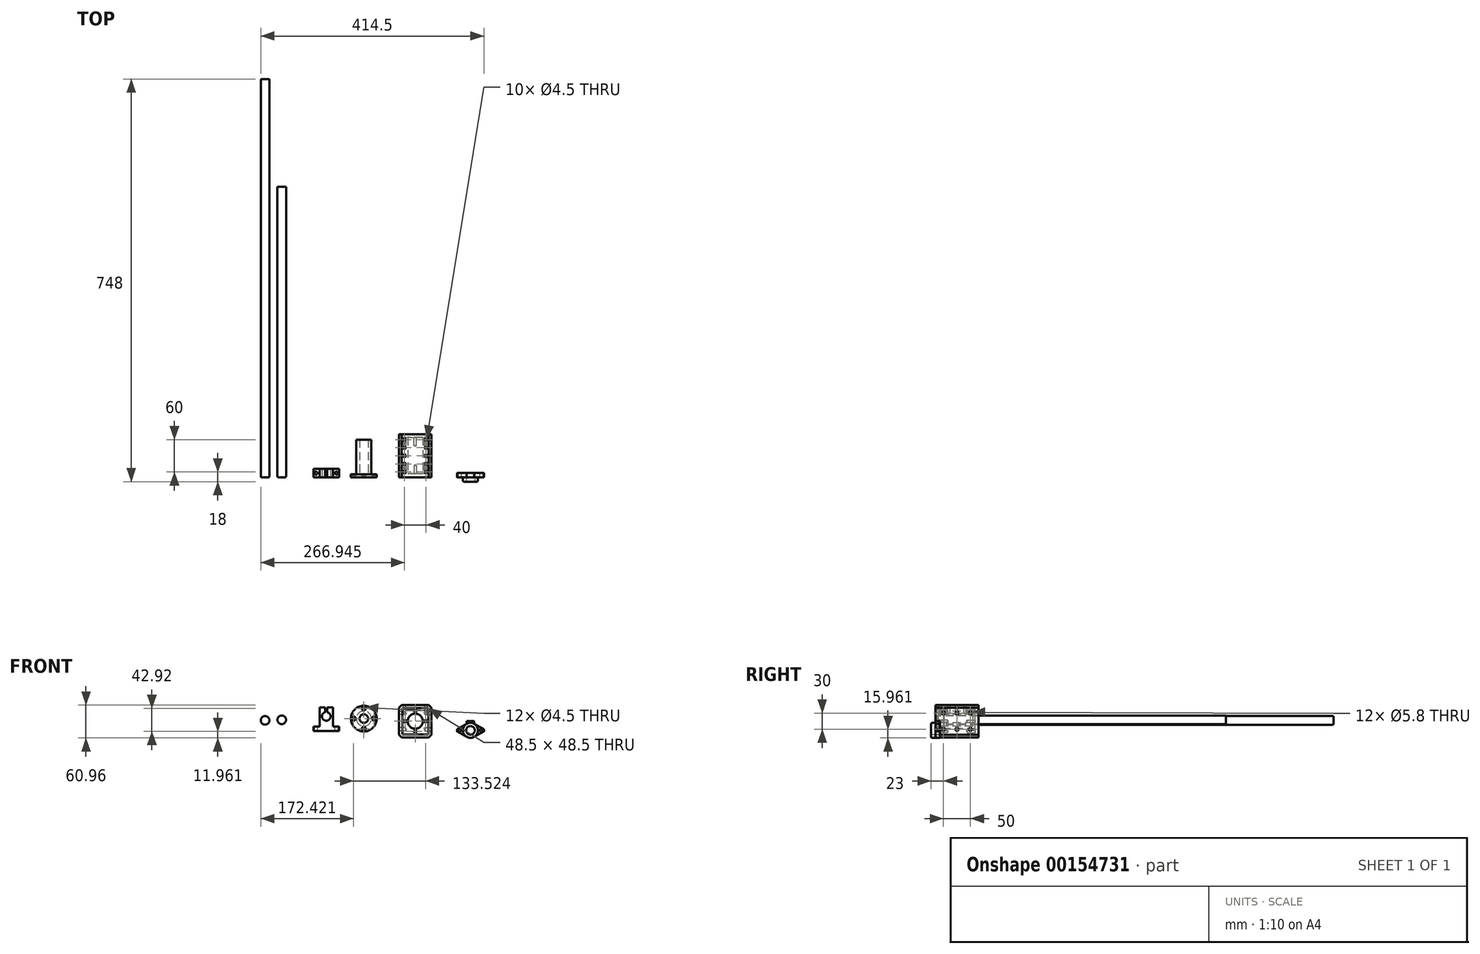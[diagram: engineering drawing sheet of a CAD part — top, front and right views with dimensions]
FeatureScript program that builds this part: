
annotation { "Feature Type Name" : "Feature", "Feature Type Description" : "" }
export const myFeature = defineFeature(function(context is Context, id is Id, definition is map)
    precondition{}
    {
        {
            var Q0;
            Q0=qCreatedBy(makeId("Front.planeOp"),FACE);
            var sketch = newSketch(context, id + "F0", { "sketchPlane" : qUnion([Q0])});
            skLineSegment(sketch, "E0.bottom", {"start": v(-58.78, 52.45) * mm, "end": v(-106.78, 52.45) * mm});
            skLineSegment(sketch, "E0.top", {"start": v(-58.78, 60.45) * mm, "end": v(-106.78, 60.45) * mm});
            skLineSegment(sketch, "E0.left", {"start": v(-58.78, 52.45) * mm, "end": v(-58.78, 60.45) * mm});
            skLineSegment(sketch, "E0.right", {"start": v(-106.78, 52.45) * mm, "end": v(-106.78, 60.45) * mm});
            skPoint(sketch, "E1.middle", {"position": v(-82.78, 52.45) * mm});
            skLineSegment(sketch, "E2.bottom", {"start": v(-70.28, 96.45) * mm, "end": v(-80.78, 96.45) * mm});
            skLineSegment(sketch, "E2.left", {"start": v(-70.28, 96.45) * mm, "end": v(-70.28, 60.45) * mm});
            skLineSegment(sketch, "E2.right", {"start": v(-95.28, 96.45) * mm, "end": v(-95.28, 60.45) * mm});
            skLineSegment(sketch, "E3", {"start": v(-82.78, 96.45) * mm, "end": v(-82.78, 52.45) * mm, "construction": true});
            skLineSegment(sketch, "E4.0", {"start": v(-58.78, 79.45) * mm, "end": v(-106.78, 79.45) * mm, "construction": true});
            skArc(sketch, "E5", {"start": v(-84.78, 87.2) * mm, "mid": v(-82.78, 71.45) * mm, "end": v(-80.78, 87.2) * mm});
            skLineSegment(sketch, "E6.0", {"start": v(-84.78, 87.2) * mm, "end": v(-84.78, 52.45) * mm, "construction": true});
            skLineSegment(sketch, "E7.0", {"start": v(-80.78, 87.2) * mm, "end": v(-80.78, 52.45) * mm, "construction": true});
            skLineSegment(sketch, "E8.trimOffspring", {"start": v(-84.78, 96.45) * mm, "end": v(-95.28, 96.45) * mm});
            skLineSegment(sketch, "E9", {"start": v(-80.78, 87.2) * mm, "end": v(-80.78, 96.45) * mm});
            skLineSegment(sketch, "E10", {"start": v(-84.78, 87.2) * mm, "end": v(-84.78, 96.45) * mm});
            skSolve(sketch);
        }
        {
            var Q0;
            Q0=makeQuery(id+"F0.imprint","IMPRINT",FACE,{"disambiguationData":[TD([[makeQuery(id+"F0.imprint","IMPRINT",EDGE,{"derivedFrom":sQuery(id+"F0.wireOp",EDGE,"E2.bottom")}),1.0]])]});
            var Q1;
            Q1=makeQuery(id+"F0.imprint","IMPRINT",FACE,{"disambiguationData":[TD([[makeQuery(id+"F0.imprint","IMPRINT",EDGE,{"derivedFrom":sQuery(id+"F0.wireOp",EDGE,"E0.bottom")}),-1.0]])]});
            extrude(context, id + "F1", {"entities" : qUnion([Q0, Q1]), "oppositeDirection" : true, "depth" : 16 * mm});
        }
        {
            var Q0;
            {var subQ0=sQuery(id+"F0.wireOp",EDGE,"E0.top");Q0=makeQuery(id+"F1.opExtrude","SWEPT_FACE",FACE,{"disambiguationData":[OSD([subQ0]),TDD([makeQuery(id+"F0.imprint","IMPRINT",EDGE,{"disambiguationData":[TD([[makeQuery(id+"F0.imprint","INTERSECT",VERTEX,{"derivedFrom":[subQ0,sQuery(id+"F0.wireOp",EDGE,"E0.right")]}),1.0]])],"derivedFrom":subQ0})])]});}
            var sketch = newSketch(context, id + "F2", { "sketchPlane" : qUnion([Q0])});
            skLineSegment(sketch, "E11", {"start": v(-106.78, 8) * mm, "end": v(-50.53, 8) * mm, "construction": true});
            skPoint(sketch, "E11.endSnap0", {"position": v(-106.78, 8) * mm});
            skLineSegment(sketch, "E12.0", {"start": v(-101.78, 16) * mm, "end": v(-101.78, 0) * mm, "construction": true});
            skLineSegment(sketch, "E13.0", {"start": v(-63.78, 16) * mm, "end": v(-63.78, 0) * mm, "construction": true});
            skCircle(sketch, "E14", {"center": v(-101.78, 8) * mm, "radius": 2.75 * mm});
            skCircle(sketch, "E15", {"center": v(-63.78, 8) * mm, "radius": 2.75 * mm});
            skSolve(sketch);
        }
        {
            var Q0;
            Q0=sQuery(id+"F2.wireOp",VERTEX,"E14.center");
            var Q1;
            Q1=sQuery(id+"F2.wireOp",VERTEX,"E15.center");
            var Q2;
            Q2=makeQuery(id+"F1.opExtrude","SWEPT_BODY",BODY,{"disambiguationData":[OSD([sQuery(id+"F0.wireOp",EDGE,"E0.bottom"),sQuery(id+"F0.wireOp",EDGE,"E0.top"),sQuery(id+"F0.wireOp",EDGE,"E0.left"),sQuery(id+"F0.wireOp",EDGE,"E0.right"),sQuery(id+"F0.wireOp",EDGE,"E2.bottom"),sQuery(id+"F0.wireOp",EDGE,"E2.left"),sQuery(id+"F0.wireOp",EDGE,"E2.right"),sQuery(id+"F0.wireOp",EDGE,"E5"),sQuery(id+"F0.wireOp",EDGE,"E8.trimOffspring"),sQuery(id+"F0.wireOp",EDGE,"E9"),sQuery(id+"F0.wireOp",EDGE,"E10")])]});
            hole(context, id + "F3", {"style" : HoleStyle.SIMPLE, "endStyle" : HoleEndStyle.THROUGH, "holeDiameter" : 5.5 * mm, "locations" : qUnion([Q0, Q1]), "scope" : qUnion([Q2]), "isTappedThrough" : true});
        }
        {
            var Q0;
            Q0=qCreatedBy(makeId("Front.planeOp"),FACE);
            var sketch = newSketch(context, id + "F4", { "sketchPlane" : qUnion([Q0])});
            skCircle(sketch, "E16", {"center": v(-196.37, 72.13) * mm, "radius": 8 * mm});
            skSolve(sketch);
        }
        {
            var Q0;
            Q0 = qSketchRegion(id + "F4", true);
            extrude(context, id + "F5", {"entities" : qUnion([Q0]), "oppositeDirection" : true, "depth" : 740 * mm});
        }
        {
            var Q0;
            Q0=makeQuery(id+"F5.opExtrude","CAP_EDGE",EDGE,{"disambiguationData":[OSD([sQuery(id+"F4.wireOp",EDGE,"E16")])],"isStart":true});
            var Q1;
            Q1=makeQuery(id+"F5.opExtrude","CAP_EDGE",EDGE,{"disambiguationData":[OSD([sQuery(id+"F4.wireOp",EDGE,"E16")])],"isStart":false});
            fillet(context, id + "F6", {"entities" : qUnion([Q0, Q1]), "radius" : 2 * mm, "tangentPropagation" : true, "allowEdgeOverflow" : false});
        }
        {
            var Q0;
            Q0=qCreatedBy(makeId("Front.planeOp"),FACE);
            var sketch = newSketch(context, id + "F7", { "sketchPlane" : qUnion([Q0])});
            skCircle(sketch, "E17", {"center": v(-12.95, 75.48) * mm, "radius": 24 * mm});
            skCircle(sketch, "E18", {"center": v(-12.95, 75.48) * mm, "radius": 19 * mm, "construction": true});
            skCircle(sketch, "E19", {"center": v(-12.95, 75.48) * mm, "radius": 8 * mm});
            skLineSegment(sketch, "E20", {"start": v(-12.95, 75.48) * mm, "end": v(-12.95, 99.79) * mm, "construction": true});
            skCircle(sketch, "E21", {"center": v(-12.95, 94.48) * mm, "radius": 3.75 * mm});
            skCircle(sketch, "E22.1.0", {"center": v(6.05, 75.48) * mm, "radius": 3.75 * mm});
            skCircle(sketch, "E22.2.0", {"center": v(-12.95, 56.48) * mm, "radius": 3.75 * mm});
            skCircle(sketch, "E22.3.0", {"center": v(-31.95, 75.48) * mm, "radius": 3.75 * mm});
            skLineSegment(sketch, "E22.anchor1", {"start": v(-12.95, 75.48) * mm, "end": v(-12.95, 94.48) * mm, "construction": true});
            skLineSegment(sketch, "E22.anchor2", {"start": v(-12.95, 75.48) * mm, "end": v(-31.95, 75.48) * mm, "construction": true});
            skCircle(sketch, "E23", {"center": v(-12.95, 75.48) * mm, "radius": 14 * mm});
            skSolve(sketch);
        }
        {
            var Q0;
            Q0=makeQuery(id+"F7.imprint","IMPRINT",FACE,{"disambiguationData":[TD([[makeQuery(id+"F7.imprint","IMPRINT",EDGE,{"derivedFrom":sQuery(id+"F7.wireOp",EDGE,"E17")}),1.0]])]});
            var Q1;
            Q1=makeQuery(id+"F7.imprint","IMPRINT",FACE,{"disambiguationData":[TD([[makeQuery(id+"F7.imprint","IMPRINT",EDGE,{"derivedFrom":sQuery(id+"F7.wireOp",EDGE,"E22.1.0")}),1.0]])]});
            var Q2;
            Q2=makeQuery(id+"F7.imprint","IMPRINT",FACE,{"disambiguationData":[TD([[makeQuery(id+"F7.imprint","IMPRINT",EDGE,{"derivedFrom":sQuery(id+"F7.wireOp",EDGE,"E22.2.0")}),1.0]])]});
            var Q3;
            Q3=makeQuery(id+"F7.imprint","IMPRINT",FACE,{"disambiguationData":[TD([[makeQuery(id+"F7.imprint","IMPRINT",EDGE,{"derivedFrom":sQuery(id+"F7.wireOp",EDGE,"E22.3.0")}),1.0]])]});
            var Q4;
            Q4=makeQuery(id+"F7.imprint","IMPRINT",FACE,{"disambiguationData":[TD([[makeQuery(id+"F7.imprint","IMPRINT",EDGE,{"derivedFrom":sQuery(id+"F7.wireOp",EDGE,"E21")}),1.0]])]});
            var Q5;
            Q5=makeQuery(id+"F7.imprint","IMPRINT",FACE,{"disambiguationData":[TD([[makeQuery(id+"F7.imprint","IMPRINT",EDGE,{"derivedFrom":sQuery(id+"F7.wireOp",EDGE,"E19")}),-1.0]])]});
            extrude(context, id + "F8", {"entities" : qUnion([Q0, Q1, Q2, Q3, Q4, Q5]), "oppositeDirection" : true, "depth" : 6 * mm});
        }
        {
            var Q0;
            Q0=makeQuery(id+"F7.imprint","IMPRINT",FACE,{"disambiguationData":[TD([[makeQuery(id+"F7.imprint","IMPRINT",EDGE,{"derivedFrom":sQuery(id+"F7.wireOp",EDGE,"E19")}),-1.0]])]});
            extrude(context, id + "F9", {"entities" : qUnion([Q0]), "operationType" : NewBodyOperationType.ADD, "oppositeDirection" : true, "depth" : 70 * mm});
        }
        {
            var Q0;
            Q0=sQuery(id+"F7.wireOp",VERTEX,"E21.center");
            var Q1;
            Q1=sQuery(id+"F7.wireOp",VERTEX,"E22.1.0.center");
            var Q2;
            Q2=sQuery(id+"F7.wireOp",VERTEX,"E22.2.0.center");
            var Q3;
            Q3=sQuery(id+"F7.wireOp",VERTEX,"E22.anchor2.end");
            var Q4;
            Q4=makeQuery(id+"F8.opExtrude","SWEPT_BODY",BODY,{"disambiguationData":[OSD([sQuery(id+"F7.wireOp",EDGE,"E17"),sQuery(id+"F7.wireOp",EDGE,"E19")])]});
            hole(context, id + "F10", {"style" : HoleStyle.C_BORE, "endStyle" : HoleEndStyle.THROUGH, "holeDiameter" : 4.5 * mm, "cBoreDiameter" : 7.5 * mm, "cBoreDepth" : 4.1 * mm, "locations" : qUnion([Q0, Q1, Q2, Q3]), "scope" : qUnion([Q4]), "isTappedThrough" : true});
        }
        {
            var Q0;
            Q0=qCreatedBy(makeId("Front.planeOp"),FACE);
            var sketch = newSketch(context, id + "F11", { "sketchPlane" : qUnion([Q0])});
            skCircle(sketch, "E24", {"center": v(82.57, 70.56) * mm, "radius": 24 * mm});
            skCircle(sketch, "E25", {"center": v(82.57, 70.56) * mm, "radius": 19 * mm, "construction": true});
            skCircle(sketch, "E26", {"center": v(82.57, 70.56) * mm, "radius": 8 * mm});
            skLineSegment(sketch, "E27", {"start": v(82.57, 70.56) * mm, "end": v(82.57, 94.81) * mm, "construction": true});
            skCircle(sketch, "E28", {"center": v(82.57, 89.56) * mm, "radius": 3.75 * mm});
            skCircle(sketch, "E29.1.0", {"center": v(101.57, 70.56) * mm, "radius": 3.75 * mm});
            skCircle(sketch, "E29.2.0", {"center": v(82.57, 51.56) * mm, "radius": 3.75 * mm});
            skCircle(sketch, "E29.3.0", {"center": v(63.57, 70.56) * mm, "radius": 3.75 * mm});
            skLineSegment(sketch, "E29.anchor1", {"start": v(82.57, 70.56) * mm, "end": v(82.57, 89.56) * mm, "construction": true});
            skLineSegment(sketch, "E29.anchor2", {"start": v(82.57, 70.56) * mm, "end": v(63.57, 70.56) * mm, "construction": true});
            skCircle(sketch, "E30", {"center": v(82.57, 70.56) * mm, "radius": 14 * mm});
            skLineSegment(sketch, "E31.bottom", {"start": v(112.57, 40.56) * mm, "end": v(52.57, 40.56) * mm});
            skLineSegment(sketch, "E31.top", {"start": v(112.57, 100.56) * mm, "end": v(52.57, 100.56) * mm});
            skLineSegment(sketch, "E31.left", {"start": v(112.57, 40.56) * mm, "end": v(112.57, 100.56) * mm});
            skLineSegment(sketch, "E31.right", {"start": v(52.57, 40.56) * mm, "end": v(52.57, 100.56) * mm});
            skLineSegment(sketch, "E32.bottom", {"start": v(106.82, 94.81) * mm, "end": v(58.32, 94.81) * mm});
            skLineSegment(sketch, "E32.top", {"start": v(106.82, 46.31) * mm, "end": v(58.32, 46.31) * mm});
            skLineSegment(sketch, "E32.left", {"start": v(106.82, 94.81) * mm, "end": v(106.82, 46.31) * mm});
            skLineSegment(sketch, "E32.right", {"start": v(58.32, 94.81) * mm, "end": v(58.32, 46.31) * mm});
            skSolve(sketch);
        }
        {
            var Q0;
            Q0=makeQuery(id+"F11.imprint","IMPRINT",FACE,{"disambiguationData":[TD([[makeQuery(id+"F11.imprint","IMPRINT",EDGE,{"derivedFrom":sQuery(id+"F11.wireOp",EDGE,"E24")}),-1.0]])]});
            var Q1;
            Q1=makeQuery(id+"F11.imprint","IMPRINT",FACE,{"disambiguationData":[TD([[makeQuery(id+"F11.imprint","IMPRINT",EDGE,{"derivedFrom":sQuery(id+"F11.wireOp",EDGE,"E24")}),1.0]])]});
            var Q2;
            Q2=makeQuery(id+"F11.imprint","IMPRINT",FACE,{"disambiguationData":[TD([[makeQuery(id+"F11.imprint","IMPRINT",EDGE,{"derivedFrom":sQuery(id+"F11.wireOp",EDGE,"E28")}),1.0]])]});
            var Q3;
            Q3=makeQuery(id+"F11.imprint","IMPRINT",FACE,{"disambiguationData":[TD([[makeQuery(id+"F11.imprint","IMPRINT",EDGE,{"derivedFrom":sQuery(id+"F11.wireOp",EDGE,"E29.3.0")}),1.0]])]});
            var Q4;
            Q4=makeQuery(id+"F11.imprint","IMPRINT",FACE,{"disambiguationData":[TD([[makeQuery(id+"F11.imprint","IMPRINT",EDGE,{"derivedFrom":sQuery(id+"F11.wireOp",EDGE,"E29.2.0")}),1.0]])]});
            var Q5;
            Q5=makeQuery(id+"F11.imprint","IMPRINT",FACE,{"disambiguationData":[TD([[makeQuery(id+"F11.imprint","IMPRINT",EDGE,{"derivedFrom":sQuery(id+"F11.wireOp",EDGE,"E29.1.0")}),1.0]])]});
            var Q6;
            Q6=makeQuery(id+"F11.imprint","IMPRINT",FACE,{"disambiguationData":[TD([[makeQuery(id+"F11.imprint","IMPRINT",EDGE,{"derivedFrom":sQuery(id+"F11.wireOp",EDGE,"E31.bottom")}),-1.0]])]});
            extrude(context, id + "F12", {"entities" : qUnion([Q0, Q1, Q2, Q3, Q4, Q5, Q6]), "oppositeDirection" : true, "depth" : 80 * mm});
        }
        {
            var Q0;
            Q0=makeQuery(id+"F11.imprint","IMPRINT",FACE,{"disambiguationData":[TD([[makeQuery(id+"F11.imprint","IMPRINT",EDGE,{"derivedFrom":sQuery(id+"F11.wireOp",EDGE,"E24")}),1.0]])]});
            var Q1;
            Q1=makeQuery(id+"F11.imprint","IMPRINT",FACE,{"disambiguationData":[TD([[makeQuery(id+"F11.imprint","IMPRINT",EDGE,{"derivedFrom":sQuery(id+"F11.wireOp",EDGE,"E29.1.0")}),1.0]])]});
            var Q2;
            Q2=makeQuery(id+"F11.imprint","IMPRINT",FACE,{"disambiguationData":[TD([[makeQuery(id+"F11.imprint","IMPRINT",EDGE,{"derivedFrom":sQuery(id+"F11.wireOp",EDGE,"E28")}),1.0]])]});
            var Q3;
            Q3=makeQuery(id+"F11.imprint","IMPRINT",FACE,{"disambiguationData":[TD([[makeQuery(id+"F11.imprint","IMPRINT",EDGE,{"derivedFrom":sQuery(id+"F11.wireOp",EDGE,"E29.2.0")}),1.0]])]});
            var Q4;
            Q4=makeQuery(id+"F11.imprint","IMPRINT",FACE,{"disambiguationData":[TD([[makeQuery(id+"F11.imprint","IMPRINT",EDGE,{"derivedFrom":sQuery(id+"F11.wireOp",EDGE,"E29.3.0")}),1.0]])]});
            var Q5;
            Q5=makeQuery(id+"F11.imprint","IMPRINT",FACE,{"disambiguationData":[TD([[makeQuery(id+"F11.imprint","IMPRINT",EDGE,{"derivedFrom":sQuery(id+"F11.wireOp",EDGE,"E24")}),-1.0]])]});
            extrude(context, id + "F13", {"entities" : qUnion([Q0, Q1, Q2, Q3, Q4, Q5]), "operationType" : NewBodyOperationType.REMOVE, "oppositeDirection" : true, "depth" : 7 * mm});
        }
        {
            var Q0;
            Q0=makeQuery(id+"F13.boolean.opBoolean","COPY",FACE,{"derivedFrom":makeQuery(id+"F13.opExtrude","CAP_FACE",FACE,{"disambiguationData":[OSD([sQuery(id+"F11.wireOp",EDGE,"E24"),sQuery(id+"F11.wireOp",EDGE,"E30")])],"isStart":false})});
            var sketch = newSketch(context, id + "F14", { "sketchPlane" : qUnion([Q0])});
            skLineSegment(sketch, "E33", {"start": v(82.57, 70.56) * mm, "end": v(82.57, 94.56) * mm, "construction": true});
            skCircle(sketch, "E34", {"center": v(82.57, 70.56) * mm, "radius": 19 * mm, "construction": true});
            skCircle(sketch, "E35", {"center": v(82.57, 89.56) * mm, "radius": 2.25 * mm});
            skCircle(sketch, "E36.1.0", {"center": v(63.57, 70.56) * mm, "radius": 2.25 * mm});
            skCircle(sketch, "E36.2.0", {"center": v(82.57, 51.56) * mm, "radius": 2.25 * mm});
            skCircle(sketch, "E36.3.0", {"center": v(101.57, 70.56) * mm, "radius": 2.25 * mm});
            skSolve(sketch);
        }
        {
            var Q0;
            Q0=sQuery(id+"F14.wireOp",VERTEX,"E35.center");
            var Q1;
            Q1=sQuery(id+"F14.wireOp",VERTEX,"E36.3.0.center");
            var Q2;
            Q2=sQuery(id+"F14.wireOp",VERTEX,"E36.2.0.center");
            var Q3;
            Q3=sQuery(id+"F14.wireOp",VERTEX,"E36.1.0.center");
            var Q4;
            Q4=makeQuery(id+"F12.opExtrude","SWEPT_BODY",BODY,{"disambiguationData":[OSD([sQuery(id+"F11.wireOp",EDGE,"E30"),sQuery(id+"F11.wireOp",EDGE,"E31.bottom"),sQuery(id+"F11.wireOp",EDGE,"E31.top"),sQuery(id+"F11.wireOp",EDGE,"E31.left"),sQuery(id+"F11.wireOp",EDGE,"E31.right")])]});
            hole(context, id + "F15", {"style" : HoleStyle.SIMPLE, "endStyle" : HoleEndStyle.BLIND, "holeDiameter" : 4.5 * mm, "holeDepth" : 15 * mm, "locations" : qUnion([Q0, Q1, Q2, Q3]), "scope" : qUnion([Q4])});
        }
        {
            var Q0;
            Q0=makeQuery(id+"F12.opExtrude","CAP_FACE",FACE,{"disambiguationData":[OSD([sQuery(id+"F11.wireOp",EDGE,"E30"),sQuery(id+"F11.wireOp",EDGE,"E31.bottom"),sQuery(id+"F11.wireOp",EDGE,"E31.top"),sQuery(id+"F11.wireOp",EDGE,"E31.left"),sQuery(id+"F11.wireOp",EDGE,"E31.right")])],"isStart":false});
            var sketch = newSketch(context, id + "F16", { "sketchPlane" : qUnion([Q0])});
            skLineSegment(sketch, "E37.bottom", {"start": v(-58.32, 46.31) * mm, "end": v(-106.82, 46.31) * mm});
            skLineSegment(sketch, "E37.top", {"start": v(-58.32, 94.81) * mm, "end": v(-106.82, 94.81) * mm});
            skLineSegment(sketch, "E37.left", {"start": v(-58.32, 46.31) * mm, "end": v(-58.32, 94.81) * mm});
            skLineSegment(sketch, "E37.right", {"start": v(-106.82, 46.31) * mm, "end": v(-106.82, 94.81) * mm});
            skPoint(sketch, "E37.middle", {"position": v(-82.57, 70.56) * mm});
            skSolve(sketch);
        }
        {
            var Q0;
            Q0=makeQuery(id+"F16.imprint","IMPRINT",FACE,{"disambiguationData":[TD([[makeQuery(id+"F16.imprint","IMPRINT",EDGE,{"derivedFrom":sQuery(id+"F16.wireOp",EDGE,"E37.bottom")}),-1.0]])]});
            extrude(context, id + "F17", {"entities" : qUnion([Q0]), "operationType" : NewBodyOperationType.REMOVE, "oppositeDirection" : true, "depth" : 6 * mm});
        }
        {
            var Q0;
            Q0=makeQuery(id+"F17.boolean.opBoolean","COPY",FACE,{"derivedFrom":makeQuery(id+"F17.opExtrude","CAP_FACE",FACE,{"disambiguationData":[OSD([sQuery(id+"F11.wireOp",EDGE,"E30"),sQuery(id+"F16.wireOp",EDGE,"E37.bottom"),sQuery(id+"F16.wireOp",EDGE,"E37.top"),sQuery(id+"F16.wireOp",EDGE,"E37.left"),sQuery(id+"F16.wireOp",EDGE,"E37.right")])],"isStart":false})});
            var sketch = newSketch(context, id + "F18", { "sketchPlane" : qUnion([Q0])});
            skCircle(sketch, "E38", {"center": v(-82.57, 70.56) * mm, "radius": 19 * mm, "construction": true});
            skLineSegment(sketch, "E39", {"start": v(-82.57, 70.56) * mm, "end": v(-82.57, 94.81) * mm, "construction": true});
            skCircle(sketch, "E40", {"center": v(-82.57, 89.56) * mm, "radius": 2.74 * mm});
            skCircle(sketch, "E41.1.0", {"center": v(-101.57, 70.56) * mm, "radius": 2.74 * mm});
            skCircle(sketch, "E41.2.0", {"center": v(-82.57, 51.56) * mm, "radius": 2.74 * mm});
            skCircle(sketch, "E41.3.0", {"center": v(-63.57, 70.56) * mm, "radius": 2.74 * mm});
            skSolve(sketch);
        }
        {
            var Q0;
            Q0=sQuery(id+"F18.wireOp",VERTEX,"E40.center");
            var Q1;
            Q1=sQuery(id+"F18.wireOp",VERTEX,"E41.3.0.center");
            var Q2;
            Q2=sQuery(id+"F18.wireOp",VERTEX,"E41.2.0.center");
            var Q3;
            Q3=sQuery(id+"F18.wireOp",VERTEX,"E41.1.0.center");
            var Q4;
            Q4=makeQuery(id+"F12.opExtrude","SWEPT_BODY",BODY,{"disambiguationData":[OSD([sQuery(id+"F11.wireOp",EDGE,"E30"),sQuery(id+"F11.wireOp",EDGE,"E31.bottom"),sQuery(id+"F11.wireOp",EDGE,"E31.top"),sQuery(id+"F11.wireOp",EDGE,"E31.left"),sQuery(id+"F11.wireOp",EDGE,"E31.right")])]});
            hole(context, id + "F19", {"style" : HoleStyle.SIMPLE, "endStyle" : HoleEndStyle.BLIND, "holeDiameter" : 4.5 * mm, "holeDepth" : 15 * mm, "locations" : qUnion([Q0, Q1, Q2, Q3]), "scope" : qUnion([Q4])});
        }
        {
            var Q0;
            Q0=makeQuery(id+"F12.opExtrude","SWEPT_FACE",FACE,{"disambiguationData":[OSD([sQuery(id+"F11.wireOp",EDGE,"E31.top")])]});
            var sketch = newSketch(context, id + "F20", { "sketchPlane" : qUnion([Q0])});
            skLineSegment(sketch, "E42.bottom", {"start": v(52.57, 80) * mm, "end": v(112.57, 80) * mm});
            skLineSegment(sketch, "E42.top", {"start": v(52.57, 0) * mm, "end": v(112.57, 0) * mm});
            skLineSegment(sketch, "E42.left", {"start": v(52.57, 80) * mm, "end": v(52.57, 0) * mm});
            skLineSegment(sketch, "E42.right", {"start": v(112.57, 80) * mm, "end": v(112.57, 0) * mm});
            skLineSegment(sketch, "E43.0", {"start": v(52.57, 70) * mm, "end": v(112.57, 70) * mm, "construction": true});
            skLineSegment(sketch, "E44.0", {"start": v(62.57, 80) * mm, "end": v(62.57, 0) * mm, "construction": true});
            skCircle(sketch, "E45", {"center": v(62.57, 70) * mm, "radius": 2.75 * mm});
            skCircle(sketch, "E46.0.1.0", {"center": v(62.57, 55) * mm, "radius": 2.75 * mm});
            skCircle(sketch, "E46.0.2.0", {"center": v(62.57, 40) * mm, "radius": 2.75 * mm});
            skCircle(sketch, "E46.0.3.0", {"center": v(62.57, 25) * mm, "radius": 2.75 * mm});
            skCircle(sketch, "E46.0.4.0", {"center": v(62.57, 10) * mm, "radius": 2.75 * mm});
            skCircle(sketch, "E46.1.0.0", {"center": v(102.57, 70) * mm, "radius": 2.75 * mm});
            skCircle(sketch, "E46.1.1.0", {"center": v(102.57, 55) * mm, "radius": 2.75 * mm});
            skCircle(sketch, "E46.1.2.0", {"center": v(102.57, 40) * mm, "radius": 2.75 * mm});
            skCircle(sketch, "E46.1.3.0", {"center": v(102.57, 25) * mm, "radius": 2.75 * mm});
            skCircle(sketch, "E46.1.4.0", {"center": v(102.57, 10) * mm, "radius": 2.75 * mm});
            skLineSegment(sketch, "E46.direction1", {"start": v(62.57, 70) * mm, "end": v(102.57, 70) * mm, "construction": true});
            skLineSegment(sketch, "E46.direction2", {"start": v(62.57, 70) * mm, "end": v(62.57, 55) * mm, "construction": true});
            skSolve(sketch);
        }
        {
            var Q0;
            Q0=sQuery(id+"F20.wireOp",VERTEX,"E45.center");
            var Q1;
            Q1=sQuery(id+"F20.wireOp",VERTEX,"E46.direction2.end");
            var Q2;
            Q2=sQuery(id+"F20.wireOp",VERTEX,"E46.0.2.0.center");
            var Q3;
            Q3=sQuery(id+"F20.wireOp",VERTEX,"E46.0.3.0.center");
            var Q4;
            Q4=sQuery(id+"F20.wireOp",VERTEX,"E46.0.4.0.center");
            var Q5;
            Q5=sQuery(id+"F20.wireOp",VERTEX,"E46.1.4.0.center");
            var Q6;
            Q6=sQuery(id+"F20.wireOp",VERTEX,"E46.1.3.0.center");
            var Q7;
            Q7=sQuery(id+"F20.wireOp",VERTEX,"E46.1.2.0.center");
            var Q8;
            Q8=sQuery(id+"F20.wireOp",VERTEX,"E46.1.1.0.center");
            var Q9;
            Q9=sQuery(id+"F20.wireOp",VERTEX,"E46.direction1.end");
            var Q10;
            Q10=makeQuery(id+"F12.opExtrude","SWEPT_BODY",BODY,{"disambiguationData":[OSD([sQuery(id+"F11.wireOp",EDGE,"E30"),sQuery(id+"F11.wireOp",EDGE,"E31.bottom"),sQuery(id+"F11.wireOp",EDGE,"E31.top"),sQuery(id+"F11.wireOp",EDGE,"E31.left"),sQuery(id+"F11.wireOp",EDGE,"E31.right")])]});
            hole(context, id + "F21", {"style" : HoleStyle.SIMPLE, "endStyle" : HoleEndStyle.BLIND, "holeDiameter" : 4.5 * mm, "holeDepth" : 15 * mm, "locations" : qUnion([Q0, Q1, Q2, Q3, Q4, Q5, Q6, Q7, Q8, Q9]), "scope" : qUnion([Q10])});
        }
        {
            var Q0;
            Q0=makeQuery(id+"F12.opExtrude","SWEPT_FACE",FACE,{"disambiguationData":[OSD([sQuery(id+"F11.wireOp",EDGE,"E31.left")])]});
            var sketch = newSketch(context, id + "F22", { "sketchPlane" : qUnion([Q0])});
            skLineSegment(sketch, "E47.0", {"start": v(80, 85.56) * mm, "end": v(0, 85.56) * mm, "construction": true});
            skLineSegment(sketch, "E48.0", {"start": v(80, 55.56) * mm, "end": v(0, 55.56) * mm, "construction": true});
            skLineSegment(sketch, "E49.bottom", {"start": v(80, 100.56) * mm, "end": v(0, 100.56) * mm});
            skLineSegment(sketch, "E49.top", {"start": v(80, 40.56) * mm, "end": v(0, 40.56) * mm});
            skLineSegment(sketch, "E49.left", {"start": v(80, 100.56) * mm, "end": v(80, 40.56) * mm});
            skLineSegment(sketch, "E49.right", {"start": v(0, 100.56) * mm, "end": v(0, 40.56) * mm});
            skLineSegment(sketch, "E50.0", {"start": v(15, 100.56) * mm, "end": v(15, 40.56) * mm, "construction": true});
            skCircle(sketch, "E51", {"center": v(15, 85.56) * mm, "radius": 3 * mm});
            skCircle(sketch, "E52.0.1.0", {"center": v(15, 55.56) * mm, "radius": 3 * mm});
            skCircle(sketch, "E52.1.0.0", {"center": v(40, 85.56) * mm, "radius": 3 * mm});
            skCircle(sketch, "E52.1.1.0", {"center": v(40, 55.56) * mm, "radius": 3 * mm});
            skCircle(sketch, "E52.2.0.0", {"center": v(65, 85.56) * mm, "radius": 3 * mm});
            skCircle(sketch, "E52.2.1.0", {"center": v(65, 55.56) * mm, "radius": 3 * mm});
            skLineSegment(sketch, "E52.direction1", {"start": v(15, 85.56) * mm, "end": v(40, 85.56) * mm, "construction": true});
            skLineSegment(sketch, "E52.direction2", {"start": v(15, 85.56) * mm, "end": v(15, 55.56) * mm, "construction": true});
            skSolve(sketch);
        }
        {
            var Q0;
            Q0=sQuery(id+"F22.wireOp",VERTEX,"E51.center");
            var Q1;
            Q1=sQuery(id+"F22.wireOp",VERTEX,"E52.1.0.0.center");
            var Q2;
            Q2=sQuery(id+"F22.wireOp",VERTEX,"E52.2.0.0.center");
            var Q3;
            Q3=sQuery(id+"F22.wireOp",VERTEX,"E52.2.1.0.center");
            var Q4;
            Q4=sQuery(id+"F22.wireOp",VERTEX,"E52.1.1.0.center");
            var Q5;
            Q5=sQuery(id+"F22.wireOp",VERTEX,"E52.0.1.0.center");
            var Q6;
            Q6=makeQuery(id+"F12.opExtrude","SWEPT_BODY",BODY,{"disambiguationData":[OSD([sQuery(id+"F11.wireOp",EDGE,"E30"),sQuery(id+"F11.wireOp",EDGE,"E31.bottom"),sQuery(id+"F11.wireOp",EDGE,"E31.top"),sQuery(id+"F11.wireOp",EDGE,"E31.left"),sQuery(id+"F11.wireOp",EDGE,"E31.right")])]});
            hole(context, id + "F23", {"style" : HoleStyle.SIMPLE, "endStyle" : HoleEndStyle.BLIND, "holeDiameter" : 5.8 * mm, "holeDepth" : 12 * mm, "locations" : qUnion([Q0, Q1, Q2, Q3, Q4, Q5]), "scope" : qUnion([Q6])});
        }
        {
            var Q0;
            Q0=makeQuery(id+"F12.opExtrude","SWEPT_FACE",FACE,{"disambiguationData":[OSD([sQuery(id+"F11.wireOp",EDGE,"E31.right")])]});
            var sketch = newSketch(context, id + "F24", { "sketchPlane" : qUnion([Q0])});
            skLineSegment(sketch, "E53.bottom", {"start": v(-80, 100.56) * mm, "end": v(0, 100.56) * mm});
            skLineSegment(sketch, "E53.top", {"start": v(-80, 40.56) * mm, "end": v(0, 40.56) * mm});
            skLineSegment(sketch, "E53.left", {"start": v(-80, 100.56) * mm, "end": v(-80, 40.56) * mm});
            skLineSegment(sketch, "E53.right", {"start": v(0, 100.56) * mm, "end": v(0, 40.56) * mm});
            skLineSegment(sketch, "E54.0", {"start": v(-80, 85.56) * mm, "end": v(0, 85.56) * mm, "construction": true});
            skLineSegment(sketch, "E55.0", {"start": v(-65, 100.56) * mm, "end": v(-65, 40.56) * mm, "construction": true});
            skCircle(sketch, "E56", {"center": v(-65, 85.56) * mm, "radius": 3 * mm});
            skCircle(sketch, "E57.0.1.0", {"center": v(-65, 55.56) * mm, "radius": 3 * mm});
            skCircle(sketch, "E57.1.0.0", {"center": v(-40, 85.56) * mm, "radius": 3 * mm});
            skCircle(sketch, "E57.1.1.0", {"center": v(-40, 55.56) * mm, "radius": 3 * mm});
            skCircle(sketch, "E57.2.0.0", {"center": v(-15, 85.56) * mm, "radius": 3 * mm});
            skCircle(sketch, "E57.2.1.0", {"center": v(-15, 55.56) * mm, "radius": 3 * mm});
            skLineSegment(sketch, "E57.direction1", {"start": v(-65, 85.56) * mm, "end": v(-40, 85.56) * mm, "construction": true});
            skLineSegment(sketch, "E57.direction2", {"start": v(-65, 85.56) * mm, "end": v(-65, 55.56) * mm, "construction": true});
            skSolve(sketch);
        }
        {
            var Q0;
            Q0=sQuery(id+"F24.wireOp",VERTEX,"E57.direction1.start");
            var Q1;
            Q1=sQuery(id+"F24.wireOp",VERTEX,"E57.1.0.0.center");
            var Q2;
            Q2=sQuery(id+"F24.wireOp",VERTEX,"E57.2.0.0.center");
            var Q3;
            Q3=sQuery(id+"F24.wireOp",VERTEX,"E57.2.1.0.center");
            var Q4;
            Q4=sQuery(id+"F24.wireOp",VERTEX,"E57.1.1.0.center");
            var Q5;
            Q5=sQuery(id+"F24.wireOp",VERTEX,"E57.direction2.end");
            var Q6;
            Q6=makeQuery(id+"F12.opExtrude","SWEPT_BODY",BODY,{"disambiguationData":[OSD([sQuery(id+"F11.wireOp",EDGE,"E30"),sQuery(id+"F11.wireOp",EDGE,"E31.bottom"),sQuery(id+"F11.wireOp",EDGE,"E31.top"),sQuery(id+"F11.wireOp",EDGE,"E31.left"),sQuery(id+"F11.wireOp",EDGE,"E31.right")])]});
            hole(context, id + "F25", {"style" : HoleStyle.SIMPLE, "endStyle" : HoleEndStyle.BLIND, "holeDiameter" : 5.8 * mm, "holeDepth" : 12 * mm, "locations" : qUnion([Q0, Q1, Q2, Q3, Q4, Q5]), "scope" : qUnion([Q6])});
        }
        {
            var Q0;
            Q0=makeQuery(id+"F12.opExtrude","SWEPT_EDGE",EDGE,{"disambiguationData":[OSD([sQuery(id+"F11.wireOp",EDGE,"E31.top"),sQuery(id+"F11.wireOp",EDGE,"E31.right")])]});
            var Q1;
            Q1=makeQuery(id+"F12.opExtrude","SWEPT_EDGE",EDGE,{"disambiguationData":[OSD([sQuery(id+"F11.wireOp",EDGE,"E31.top"),sQuery(id+"F11.wireOp",EDGE,"E31.left")])]});
            var Q2;
            Q2=makeQuery(id+"F12.opExtrude","SWEPT_EDGE",EDGE,{"disambiguationData":[OSD([sQuery(id+"F11.wireOp",EDGE,"E31.bottom"),sQuery(id+"F11.wireOp",EDGE,"E31.left")])]});
            var Q3;
            Q3=makeQuery(id+"F12.opExtrude","SWEPT_EDGE",EDGE,{"disambiguationData":[OSD([sQuery(id+"F11.wireOp",EDGE,"E31.bottom"),sQuery(id+"F11.wireOp",EDGE,"E31.right")])]});
            chamfer(context, id + "F26", {"entities" : qUnion([Q0, Q1, Q2, Q3]), "width" : 5 * mm, "tangentPropagation" : true});
        }
        {
            var Q0;
            Q0=qCreatedBy(makeId("Front.planeOp"),FACE);
            var sketch = newSketch(context, id + "F27", { "sketchPlane" : qUnion([Q0])});
            skPoint(sketch, "E58.middle", {"position": v(185.13, 53.6) * mm});
            skCircle(sketch, "E59", {"center": v(185.13, 53.6) * mm, "radius": 8 * mm});
            skCircle(sketch, "E60", {"center": v(185.13, 53.6) * mm, "radius": 14 * mm});
            skLineSegment(sketch, "E61.left", {"start": v(210.13, 51.6) * mm, "end": v(210.13, 55.6) * mm});
            skLineSegment(sketch, "E61.right", {"start": v(160.13, 51.6) * mm, "end": v(160.13, 55.6) * mm});
            skCircle(sketch, "E62", {"center": v(165.13, 53.6) * mm, "radius": 2.75 * mm});
            skCircle(sketch, "E63", {"center": v(205.13, 53.6) * mm, "radius": 2.75 * mm});
            skLineSegment(sketch, "E64", {"start": v(210.13, 55.6) * mm, "end": v(192, 65.8) * mm});
            skLineSegment(sketch, "E65", {"start": v(210.13, 51.6) * mm, "end": v(192, 41.4) * mm});
            skLineSegment(sketch, "E66", {"start": v(160.13, 51.6) * mm, "end": v(178.27, 41.4) * mm});
            skLineSegment(sketch, "E67", {"start": v(160.13, 55.6) * mm, "end": v(178.27, 65.8) * mm});
            skLineSegment(sketch, "E68", {"start": v(178.27, 65.8) * mm, "end": v(178.27, 70.6) * mm});
            skLineSegment(sketch, "E69", {"start": v(192, 65.8) * mm, "end": v(192, 70.6) * mm});
            skLineSegment(sketch, "E70", {"start": v(192, 70.6) * mm, "end": v(178.27, 70.6) * mm});
            skSolve(sketch);
        }
        {
            var Q0;
            {var subQ2=sQuery(id+"F27.wireOp",EDGE,"E68");Q0=makeQuery(id+"F27.imprint","IMPRINT",FACE,{"disambiguationData":[TD([[makeQuery(id+"F27.imprint","IMPRINT",EDGE,{"derivedFrom":subQ2}),-1.0]])]});}
            var Q1;
            Q1=makeQuery(id+"F27.imprint","IMPRINT",FACE,{"disambiguationData":[TD([[makeQuery(id+"F27.imprint","IMPRINT",EDGE,{"derivedFrom":sQuery(id+"F27.wireOp",EDGE,"E61.right")}),-1.0]])]});
            var Q2;
            Q2=makeQuery(id+"F27.imprint","IMPRINT",FACE,{"disambiguationData":[TD([[makeQuery(id+"F27.imprint","IMPRINT",EDGE,{"derivedFrom":sQuery(id+"F27.wireOp",EDGE,"E59")}),-1.0]])]});
            var Q3;
            Q3=makeQuery(id+"F27.imprint","IMPRINT",FACE,{"disambiguationData":[TD([[makeQuery(id+"F27.imprint","IMPRINT",EDGE,{"derivedFrom":sQuery(id+"F27.wireOp",EDGE,"E61.left")}),1.0]])]});
            extrude(context, id + "F28", {"entities" : qUnion([Q0, Q1, Q2, Q3]), "oppositeDirection" : true, "depth" : 8 * mm});
        }
        {
            var Q0;
            Q0=makeQuery(id+"F27.imprint","IMPRINT",FACE,{"disambiguationData":[TD([[makeQuery(id+"F27.imprint","IMPRINT",EDGE,{"derivedFrom":sQuery(id+"F27.wireOp",EDGE,"E59")}),-1.0]])]});
            extrude(context, id + "F29", {"entities" : qUnion([Q0]), "operationType" : NewBodyOperationType.ADD, "depth" : 8 * mm});
        }
        {
            var Q0;
            Q0=makeQuery(id+"F29.opExtrude","CAP_EDGE",EDGE,{"disambiguationData":[OSD([sQuery(id+"F27.wireOp",EDGE,"E60")])],"isStart":false});
            fillet(context, id + "F30", {"entities" : qUnion([Q0]), "radius" : 2 * mm, "tangentPropagation" : true, "allowEdgeOverflow" : false});
        }
        {
            var Q0;
            Q0=makeQuery(id+"F28.opExtrude","CAP_EDGE",EDGE,{"disambiguationData":[OSD([sQuery(id+"F27.wireOp",EDGE,"E65")])],"isStart":true});
            var Q1;
            Q1=makeQuery(id+"F28.opExtrude","CAP_EDGE",EDGE,{"disambiguationData":[OSD([sQuery(id+"F27.wireOp",EDGE,"E64")])],"isStart":true});
            var Q2;
            Q2=makeQuery(id+"F28.opExtrude","CAP_EDGE",EDGE,{"disambiguationData":[OSD([sQuery(id+"F27.wireOp",EDGE,"E61.left")])],"isStart":true});
            var Q3;
            Q3=makeQuery(id+"F28.opExtrude","CAP_EDGE",EDGE,{"disambiguationData":[OSD([sQuery(id+"F27.wireOp",EDGE,"E66")])],"isStart":true});
            var Q4;
            Q4=makeQuery(id+"F28.opExtrude","CAP_EDGE",EDGE,{"disambiguationData":[OSD([sQuery(id+"F27.wireOp",EDGE,"E67")])],"isStart":true});
            var Q5;
            Q5=makeQuery(id+"F28.opExtrude","CAP_EDGE",EDGE,{"disambiguationData":[OSD([sQuery(id+"F27.wireOp",EDGE,"E61.right")])],"isStart":true});
            fillet(context, id + "F31", {"entities" : qUnion([Q0, Q1, Q2, Q3, Q4, Q5]), "radius" : 1 * mm, "tangentPropagation" : true, "allowEdgeOverflow" : false});
        }
        {
            var Q0;
            Q0=qCreatedBy(makeId("Front.planeOp"),FACE);
            var sketch = newSketch(context, id + "F32", { "sketchPlane" : qUnion([Q0])});
            skCircle(sketch, "E71", {"center": v(-165.51, 73.12) * mm, "radius": 8 * mm});
            skSolve(sketch);
        }
        {
            var Q0;
            Q0=makeQuery(id+"F32.imprint","IMPRINT",FACE,{"disambiguationData":[TD([[makeQuery(id+"F32.imprint","IMPRINT",EDGE,{"derivedFrom":sQuery(id+"F32.wireOp",EDGE,"E71")}),1.0]])]});
            extrude(context, id + "F33", {"entities" : qUnion([Q0]), "oppositeDirection" : true, "depth" : 540 * mm});
        }
        {
            var Q0;
            Q0=makeQuery(id+"F33.opExtrude","CAP_EDGE",EDGE,{"disambiguationData":[OSD([sQuery(id+"F32.wireOp",EDGE,"E71")])],"isStart":true});
            fillet(context, id + "F34", {"entities" : qUnion([Q0]), "radius" : 2 * mm, "tangentPropagation" : true, "allowEdgeOverflow" : false});
        }
    });
